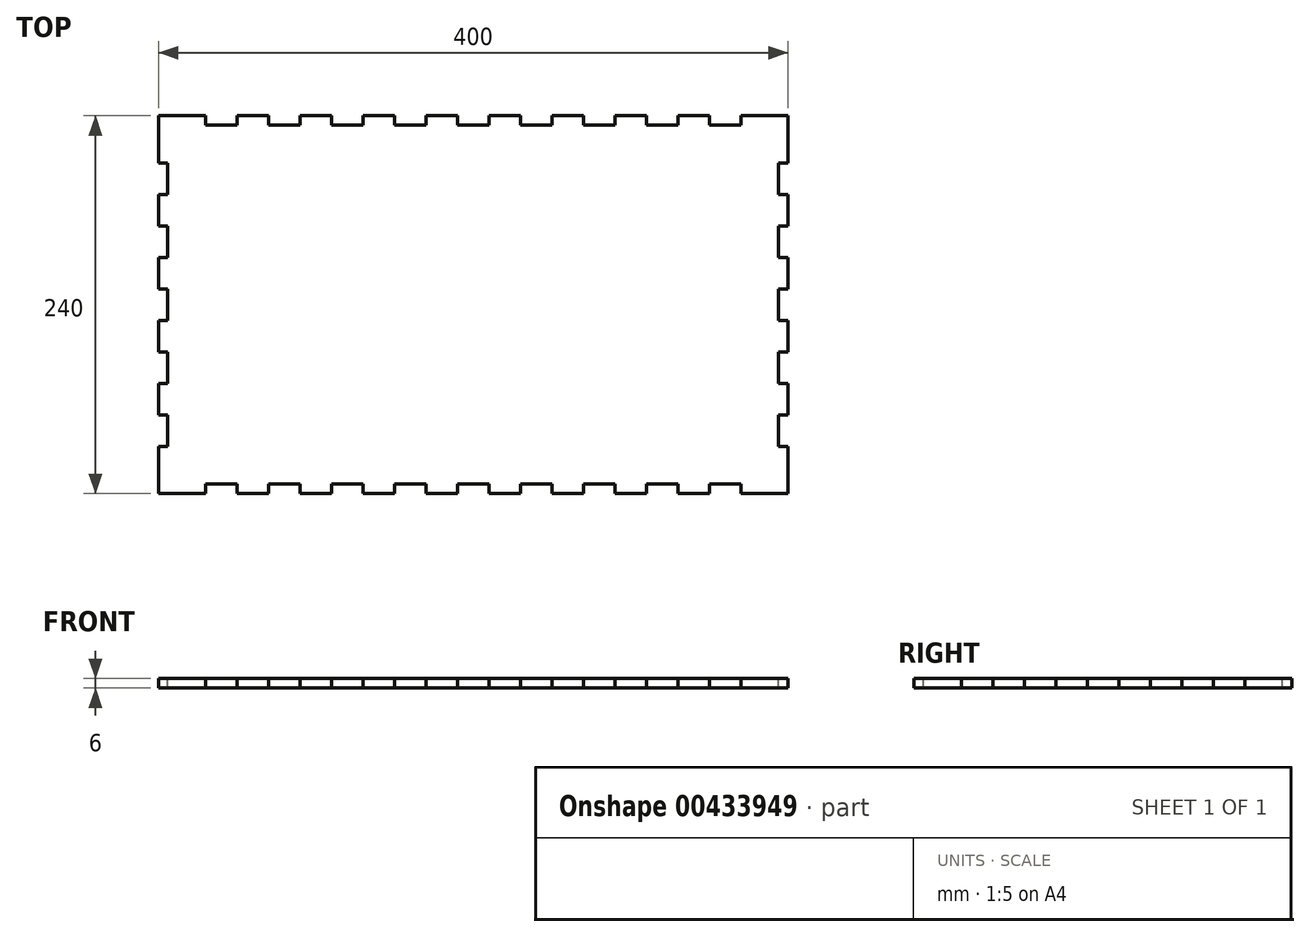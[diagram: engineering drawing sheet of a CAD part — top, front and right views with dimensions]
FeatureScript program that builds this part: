
annotation { "Feature Type Name" : "Feature", "Feature Type Description" : "" }
export const myFeature = defineFeature(function(context is Context, id is Id, definition is map)
    precondition{}
    {
        {
            var Q0;
            Q0=qCreatedBy(makeId("Top.planeOp"),FACE);
            var sketch = newSketch(context, id + "F0", { "sketchPlane" : qUnion([Q0])});
            skLineSegment(sketch, "E0.bottom", {"start": v(200, -120) * mm, "end": v(-200, -120) * mm});
            skLineSegment(sketch, "E0.top", {"start": v(200, 120) * mm, "end": v(-200, 120) * mm});
            skLineSegment(sketch, "E0.left", {"start": v(200, -120) * mm, "end": v(200, 120) * mm});
            skLineSegment(sketch, "E0.right", {"start": v(-200, -120) * mm, "end": v(-200, 120) * mm});
            skPoint(sketch, "E0.middle", {"position": v(0, 0) * mm});
            skSolve(sketch);
        }
        {
            var Q0;
            Q0=makeQuery(id+"F0.imprint","IMPRINT",FACE,{"disambiguationData":[TD([[makeQuery(id+"F0.imprint","IMPRINT",EDGE,{"derivedFrom":sQuery(id+"F0.wireOp",EDGE,"E0.bottom")}),-1.0]])]});
            extrude(context, id + "F1", {"entities" : qUnion([Q0]), "depth" : 6 * mm});
        }
        {
            var Q0;
            Q0=makeQuery(id+"F1.opExtrude","CAP_FACE",FACE,{"disambiguationData":[OSD([sQuery(id+"F0.wireOp",EDGE,"E0.bottom"),sQuery(id+"F0.wireOp",EDGE,"E0.top"),sQuery(id+"F0.wireOp",EDGE,"E0.left"),sQuery(id+"F0.wireOp",EDGE,"E0.right")])],"isStart":false});
            var sketch = newSketch(context, id + "F2", { "sketchPlane" : qUnion([Q0])});
            skLineSegment(sketch, "E1", {"start": v(-200, 90) * mm, "end": v(-194, 90) * mm});
            skLineSegment(sketch, "E2", {"start": v(-194, 90) * mm, "end": v(-194, 70) * mm});
            skLineSegment(sketch, "E3", {"start": v(-194, 70) * mm, "end": v(-200, 70) * mm});
            skLineSegment(sketch, "E4.1.0.0", {"start": v(-200, 50) * mm, "end": v(-194, 50) * mm});
            skLineSegment(sketch, "E4.1.0.1", {"start": v(-194, 50) * mm, "end": v(-194, 30) * mm});
            skLineSegment(sketch, "E4.1.0.2", {"start": v(-194, 30) * mm, "end": v(-200, 30) * mm});
            skLineSegment(sketch, "E4.2.0.0", {"start": v(-200, 10) * mm, "end": v(-194, 10) * mm});
            skLineSegment(sketch, "E4.2.0.1", {"start": v(-194, 10) * mm, "end": v(-194, -10) * mm});
            skLineSegment(sketch, "E4.2.0.2", {"start": v(-194, -10) * mm, "end": v(-200, -10) * mm});
            skLineSegment(sketch, "E4.3.0.0", {"start": v(-200, -30) * mm, "end": v(-194, -30) * mm});
            skLineSegment(sketch, "E4.3.0.1", {"start": v(-194, -30) * mm, "end": v(-194, -50) * mm});
            skLineSegment(sketch, "E4.3.0.2", {"start": v(-194, -50) * mm, "end": v(-200, -50) * mm});
            skLineSegment(sketch, "E4.4.0.0", {"start": v(-200, -70) * mm, "end": v(-194, -70) * mm});
            skLineSegment(sketch, "E4.4.0.1", {"start": v(-194, -70) * mm, "end": v(-194, -90) * mm});
            skLineSegment(sketch, "E4.4.0.2", {"start": v(-194, -90) * mm, "end": v(-200, -90) * mm});
            skLineSegment(sketch, "E4.direction1", {"start": v(-200, 100) * mm, "end": v(-200, 60) * mm, "construction": true});
            skLineSegment(sketch, "E5.MirrorCS", {"start": v(200, 90) * mm, "end": v(194, 90) * mm});
            skLineSegment(sketch, "E6.MirrorCS", {"start": v(194, -90) * mm, "end": v(200, -90) * mm});
            skLineSegment(sketch, "E7.MirrorCS", {"start": v(200, 10) * mm, "end": v(194, 10) * mm});
            skLineSegment(sketch, "E8.MirrorCS", {"start": v(200, -70) * mm, "end": v(194, -70) * mm});
            skLineSegment(sketch, "E9.MirrorCS", {"start": v(194, 30) * mm, "end": v(200, 30) * mm});
            skLineSegment(sketch, "E10.MirrorCS", {"start": v(194, -50) * mm, "end": v(200, -50) * mm});
            skLineSegment(sketch, "E11.MirrorCS", {"start": v(200, 50) * mm, "end": v(194, 50) * mm});
            skLineSegment(sketch, "E12.MirrorCS", {"start": v(194, 70) * mm, "end": v(200, 70) * mm});
            skLineSegment(sketch, "E13.MirrorCS", {"start": v(200, -30) * mm, "end": v(194, -30) * mm});
            skLineSegment(sketch, "E14.MirrorCS", {"start": v(194, -10) * mm, "end": v(200, -10) * mm});
            skLineSegment(sketch, "E15.MirrorCS", {"start": v(194, 90) * mm, "end": v(194, 70) * mm});
            skLineSegment(sketch, "E16.MirrorCS", {"start": v(194, -70) * mm, "end": v(194, -90) * mm});
            skLineSegment(sketch, "E17.MirrorCS", {"start": v(194, 50) * mm, "end": v(194, 30) * mm});
            skLineSegment(sketch, "E18.MirrorCS", {"start": v(194, -30) * mm, "end": v(194, -50) * mm});
            skLineSegment(sketch, "E19.MirrorCS", {"start": v(194, 10) * mm, "end": v(194, -10) * mm});
            skLineSegment(sketch, "E20", {"start": v(-170, 120) * mm, "end": v(-170, 114) * mm});
            skLineSegment(sketch, "E21", {"start": v(-170, 114) * mm, "end": v(-150, 114) * mm});
            skLineSegment(sketch, "E22", {"start": v(-150, 114) * mm, "end": v(-150, 120) * mm});
            skLineSegment(sketch, "E23.1.0.0", {"start": v(-130, 114) * mm, "end": v(-110, 114) * mm});
            skLineSegment(sketch, "E23.1.0.1", {"start": v(-110, 114) * mm, "end": v(-110, 120) * mm});
            skLineSegment(sketch, "E23.1.0.2", {"start": v(-130, 120) * mm, "end": v(-130, 114) * mm});
            skLineSegment(sketch, "E23.2.0.0", {"start": v(-90, 114) * mm, "end": v(-70, 114) * mm});
            skLineSegment(sketch, "E23.2.0.1", {"start": v(-70, 114) * mm, "end": v(-70, 120) * mm});
            skLineSegment(sketch, "E23.2.0.2", {"start": v(-90, 120) * mm, "end": v(-90, 114) * mm});
            skLineSegment(sketch, "E23.3.0.0", {"start": v(-50, 114) * mm, "end": v(-30, 114) * mm});
            skLineSegment(sketch, "E23.3.0.1", {"start": v(-30, 114) * mm, "end": v(-30, 120) * mm});
            skLineSegment(sketch, "E23.3.0.2", {"start": v(-50, 120) * mm, "end": v(-50, 114) * mm});
            skLineSegment(sketch, "E23.4.0.0", {"start": v(-10, 114) * mm, "end": v(10, 114) * mm});
            skLineSegment(sketch, "E23.4.0.1", {"start": v(10, 114) * mm, "end": v(10, 120) * mm});
            skLineSegment(sketch, "E23.4.0.2", {"start": v(-10, 120) * mm, "end": v(-10, 114) * mm});
            skLineSegment(sketch, "E23.5.0.0", {"start": v(30, 114) * mm, "end": v(50, 114) * mm});
            skLineSegment(sketch, "E23.5.0.1", {"start": v(50, 114) * mm, "end": v(50, 120) * mm});
            skLineSegment(sketch, "E23.5.0.2", {"start": v(30, 120) * mm, "end": v(30, 114) * mm});
            skLineSegment(sketch, "E23.6.0.0", {"start": v(70, 114) * mm, "end": v(90, 114) * mm});
            skLineSegment(sketch, "E23.6.0.1", {"start": v(90, 114) * mm, "end": v(90, 120) * mm});
            skLineSegment(sketch, "E23.6.0.2", {"start": v(70, 120) * mm, "end": v(70, 114) * mm});
            skLineSegment(sketch, "E23.7.0.0", {"start": v(110, 114) * mm, "end": v(130, 114) * mm});
            skLineSegment(sketch, "E23.7.0.1", {"start": v(130, 114) * mm, "end": v(130, 120) * mm});
            skLineSegment(sketch, "E23.7.0.2", {"start": v(110, 120) * mm, "end": v(110, 114) * mm});
            skLineSegment(sketch, "E23.8.0.0", {"start": v(150, 114) * mm, "end": v(170, 114) * mm});
            skLineSegment(sketch, "E23.8.0.1", {"start": v(170, 114) * mm, "end": v(170, 120) * mm});
            skLineSegment(sketch, "E23.8.0.2", {"start": v(150, 120) * mm, "end": v(150, 114) * mm});
            skLineSegment(sketch, "E23.direction1", {"start": v(-170, 114) * mm, "end": v(-130, 114) * mm, "construction": true});
            skLineSegment(sketch, "E24.MirrorCS", {"start": v(-130, -120) * mm, "end": v(-130, -114) * mm});
            skLineSegment(sketch, "E25.MirrorCS", {"start": v(-170, -120) * mm, "end": v(-170, -114) * mm});
            skLineSegment(sketch, "E26.MirrorCS", {"start": v(70, -120) * mm, "end": v(70, -114) * mm});
            skLineSegment(sketch, "E27.MirrorCS", {"start": v(-110, -114) * mm, "end": v(-110, -120) * mm});
            skLineSegment(sketch, "E28.MirrorCS", {"start": v(-50, -120) * mm, "end": v(-50, -114) * mm});
            skLineSegment(sketch, "E29.MirrorCS", {"start": v(90, -114) * mm, "end": v(90, -120) * mm});
            skLineSegment(sketch, "E30.MirrorCS", {"start": v(-30, -114) * mm, "end": v(-30, -120) * mm});
            skLineSegment(sketch, "E31.MirrorCS", {"start": v(150, -120) * mm, "end": v(150, -114) * mm});
            skLineSegment(sketch, "E32.MirrorCS", {"start": v(170, -114) * mm, "end": v(170, -120) * mm});
            skLineSegment(sketch, "E33.MirrorCS", {"start": v(-10, -120) * mm, "end": v(-10, -114) * mm});
            skLineSegment(sketch, "E34.MirrorCS", {"start": v(-150, -114) * mm, "end": v(-150, -120) * mm});
            skLineSegment(sketch, "E35.MirrorCS", {"start": v(10, -114) * mm, "end": v(10, -120) * mm});
            skLineSegment(sketch, "E36.MirrorCS", {"start": v(-90, -120) * mm, "end": v(-90, -114) * mm});
            skLineSegment(sketch, "E37.MirrorCS", {"start": v(30, -120) * mm, "end": v(30, -114) * mm});
            skLineSegment(sketch, "E38.MirrorCS", {"start": v(110, -120) * mm, "end": v(110, -114) * mm});
            skLineSegment(sketch, "E39.MirrorCS", {"start": v(50, -114) * mm, "end": v(50, -120) * mm});
            skLineSegment(sketch, "E40.MirrorCS", {"start": v(-70, -114) * mm, "end": v(-70, -120) * mm});
            skLineSegment(sketch, "E41.MirrorCS", {"start": v(130, -114) * mm, "end": v(130, -120) * mm});
            skLineSegment(sketch, "E42.MirrorCS", {"start": v(-170, -114) * mm, "end": v(-150, -114) * mm});
            skLineSegment(sketch, "E43.MirrorCS", {"start": v(-170, -114) * mm, "end": v(-130, -114) * mm, "construction": true});
            skLineSegment(sketch, "E44.MirrorCS", {"start": v(-130, -114) * mm, "end": v(-110, -114) * mm});
            skLineSegment(sketch, "E45.MirrorCS", {"start": v(-50, -114) * mm, "end": v(-30, -114) * mm});
            skLineSegment(sketch, "E46.MirrorCS", {"start": v(-10, -114) * mm, "end": v(10, -114) * mm});
            skLineSegment(sketch, "E47.MirrorCS", {"start": v(110, -114) * mm, "end": v(130, -114) * mm});
            skLineSegment(sketch, "E48.MirrorCS", {"start": v(-90, -114) * mm, "end": v(-70, -114) * mm});
            skLineSegment(sketch, "E49.MirrorCS", {"start": v(150, -114) * mm, "end": v(170, -114) * mm});
            skLineSegment(sketch, "E50.MirrorCS", {"start": v(70, -114) * mm, "end": v(90, -114) * mm});
            skLineSegment(sketch, "E51.MirrorCS", {"start": v(30, -114) * mm, "end": v(50, -114) * mm});
            skSolve(sketch);
        }
        {
            var Q0;
            {var subQ0=sQuery(id+"F2.wireOp",EDGE,"E1");Q0=makeQuery(id+"F2.imprint","IMPRINT",FACE,{"disambiguationData":[TD([[makeQuery(id+"F2.imprint","IMPRINT",EDGE,{"derivedFrom":subQ0}),-1.0]])]});}
            var Q1;
            {var subQ0=sQuery(id+"F2.wireOp",EDGE,"E4.1.0.0");Q1=makeQuery(id+"F2.imprint","IMPRINT",FACE,{"disambiguationData":[TD([[makeQuery(id+"F2.imprint","IMPRINT",EDGE,{"derivedFrom":subQ0}),-1.0]])]});}
            var Q2;
            {var subQ0=sQuery(id+"F2.wireOp",EDGE,"E4.3.0.0");Q2=makeQuery(id+"F2.imprint","IMPRINT",FACE,{"disambiguationData":[TD([[makeQuery(id+"F2.imprint","IMPRINT",EDGE,{"derivedFrom":subQ0}),-1.0]])]});}
            var Q3;
            {var subQ0=sQuery(id+"F2.wireOp",EDGE,"E4.2.0.0");Q3=makeQuery(id+"F2.imprint","IMPRINT",FACE,{"disambiguationData":[TD([[makeQuery(id+"F2.imprint","IMPRINT",EDGE,{"derivedFrom":subQ0}),-1.0]])]});}
            var Q4;
            {var subQ0=sQuery(id+"F2.wireOp",EDGE,"E4.4.0.0");Q4=makeQuery(id+"F2.imprint","IMPRINT",FACE,{"disambiguationData":[TD([[makeQuery(id+"F2.imprint","IMPRINT",EDGE,{"derivedFrom":subQ0}),-1.0]])]});}
            var Q5;
            {var subQ0=sQuery(id+"F2.wireOp",EDGE,"E20");Q5=makeQuery(id+"F2.imprint","IMPRINT",FACE,{"disambiguationData":[TD([[makeQuery(id+"F2.imprint","IMPRINT",EDGE,{"derivedFrom":subQ0}),1.0]])]});}
            var Q6;
            Q6=makeQuery(id+"F2.imprint","IMPRINT",FACE,{"disambiguationData":[TD([[makeQuery(id+"F2.imprint","IMPRINT",EDGE,{"derivedFrom":sQuery(id+"F2.wireOp",EDGE,"E23.1.0.0")}),1.0]])]});
            var Q7;
            Q7=makeQuery(id+"F2.imprint","IMPRINT",FACE,{"disambiguationData":[TD([[makeQuery(id+"F2.imprint","IMPRINT",EDGE,{"derivedFrom":sQuery(id+"F2.wireOp",EDGE,"E23.2.0.0")}),1.0]])]});
            var Q8;
            Q8=makeQuery(id+"F2.imprint","IMPRINT",FACE,{"disambiguationData":[TD([[makeQuery(id+"F2.imprint","IMPRINT",EDGE,{"derivedFrom":sQuery(id+"F2.wireOp",EDGE,"E23.3.0.0")}),1.0]])]});
            var Q9;
            Q9=makeQuery(id+"F2.imprint","IMPRINT",FACE,{"disambiguationData":[TD([[makeQuery(id+"F2.imprint","IMPRINT",EDGE,{"derivedFrom":sQuery(id+"F2.wireOp",EDGE,"E23.4.0.0")}),1.0]])]});
            var Q10;
            Q10=makeQuery(id+"F2.imprint","IMPRINT",FACE,{"disambiguationData":[TD([[makeQuery(id+"F2.imprint","IMPRINT",EDGE,{"derivedFrom":sQuery(id+"F2.wireOp",EDGE,"E23.5.0.0")}),1.0]])]});
            var Q11;
            Q11=makeQuery(id+"F2.imprint","IMPRINT",FACE,{"disambiguationData":[TD([[makeQuery(id+"F2.imprint","IMPRINT",EDGE,{"derivedFrom":sQuery(id+"F2.wireOp",EDGE,"E23.6.0.0")}),1.0]])]});
            var Q12;
            Q12=makeQuery(id+"F2.imprint","IMPRINT",FACE,{"disambiguationData":[TD([[makeQuery(id+"F2.imprint","IMPRINT",EDGE,{"derivedFrom":sQuery(id+"F2.wireOp",EDGE,"E23.7.0.0")}),1.0]])]});
            var Q13;
            Q13=makeQuery(id+"F2.imprint","IMPRINT",FACE,{"disambiguationData":[TD([[makeQuery(id+"F2.imprint","IMPRINT",EDGE,{"derivedFrom":sQuery(id+"F2.wireOp",EDGE,"E23.8.0.0")}),1.0]])]});
            var Q14;
            {var subQ0=sQuery(id+"F2.wireOp",EDGE,"E5.MirrorCS");Q14=makeQuery(id+"F2.imprint","IMPRINT",FACE,{"disambiguationData":[TD([[makeQuery(id+"F2.imprint","IMPRINT",EDGE,{"derivedFrom":subQ0}),1.0]])]});}
            var Q15;
            {var subQ0=sQuery(id+"F2.wireOp",EDGE,"E9.MirrorCS");Q15=makeQuery(id+"F2.imprint","IMPRINT",FACE,{"disambiguationData":[TD([[makeQuery(id+"F2.imprint","IMPRINT",EDGE,{"derivedFrom":subQ0}),1.0]])]});}
            var Q16;
            {var subQ0=sQuery(id+"F2.wireOp",EDGE,"E7.MirrorCS");Q16=makeQuery(id+"F2.imprint","IMPRINT",FACE,{"disambiguationData":[TD([[makeQuery(id+"F2.imprint","IMPRINT",EDGE,{"derivedFrom":subQ0}),1.0]])]});}
            var Q17;
            {var subQ0=sQuery(id+"F2.wireOp",EDGE,"E10.MirrorCS");Q17=makeQuery(id+"F2.imprint","IMPRINT",FACE,{"disambiguationData":[TD([[makeQuery(id+"F2.imprint","IMPRINT",EDGE,{"derivedFrom":subQ0}),1.0]])]});}
            var Q18;
            {var subQ0=sQuery(id+"F2.wireOp",EDGE,"E6.MirrorCS");Q18=makeQuery(id+"F2.imprint","IMPRINT",FACE,{"disambiguationData":[TD([[makeQuery(id+"F2.imprint","IMPRINT",EDGE,{"derivedFrom":subQ0}),1.0]])]});}
            var Q19;
            {var subQ0=sQuery(id+"F2.wireOp",EDGE,"E25.MirrorCS");Q19=makeQuery(id+"F2.imprint","IMPRINT",FACE,{"disambiguationData":[TD([[makeQuery(id+"F2.imprint","IMPRINT",EDGE,{"derivedFrom":subQ0}),-1.0]])]});}
            var Q20;
            {var subQ0=sQuery(id+"F2.wireOp",EDGE,"E24.MirrorCS");Q20=makeQuery(id+"F2.imprint","IMPRINT",FACE,{"disambiguationData":[TD([[makeQuery(id+"F2.imprint","IMPRINT",EDGE,{"derivedFrom":subQ0}),-1.0]])]});}
            var Q21;
            {var subQ0=sQuery(id+"F2.wireOp",EDGE,"E36.MirrorCS");Q21=makeQuery(id+"F2.imprint","IMPRINT",FACE,{"disambiguationData":[TD([[makeQuery(id+"F2.imprint","IMPRINT",EDGE,{"derivedFrom":subQ0}),-1.0]])]});}
            var Q22;
            {var subQ0=sQuery(id+"F2.wireOp",EDGE,"E28.MirrorCS");Q22=makeQuery(id+"F2.imprint","IMPRINT",FACE,{"disambiguationData":[TD([[makeQuery(id+"F2.imprint","IMPRINT",EDGE,{"derivedFrom":subQ0}),-1.0]])]});}
            var Q23;
            {var subQ0=sQuery(id+"F2.wireOp",EDGE,"E33.MirrorCS");Q23=makeQuery(id+"F2.imprint","IMPRINT",FACE,{"disambiguationData":[TD([[makeQuery(id+"F2.imprint","IMPRINT",EDGE,{"derivedFrom":subQ0}),-1.0]])]});}
            var Q24;
            {var subQ0=sQuery(id+"F2.wireOp",EDGE,"E37.MirrorCS");Q24=makeQuery(id+"F2.imprint","IMPRINT",FACE,{"disambiguationData":[TD([[makeQuery(id+"F2.imprint","IMPRINT",EDGE,{"derivedFrom":subQ0}),-1.0]])]});}
            var Q25;
            {var subQ0=sQuery(id+"F2.wireOp",EDGE,"E26.MirrorCS");Q25=makeQuery(id+"F2.imprint","IMPRINT",FACE,{"disambiguationData":[TD([[makeQuery(id+"F2.imprint","IMPRINT",EDGE,{"derivedFrom":subQ0}),-1.0]])]});}
            var Q26;
            {var subQ0=sQuery(id+"F2.wireOp",EDGE,"E38.MirrorCS");Q26=makeQuery(id+"F2.imprint","IMPRINT",FACE,{"disambiguationData":[TD([[makeQuery(id+"F2.imprint","IMPRINT",EDGE,{"derivedFrom":subQ0}),-1.0]])]});}
            var Q27;
            {var subQ0=sQuery(id+"F2.wireOp",EDGE,"E31.MirrorCS");Q27=makeQuery(id+"F2.imprint","IMPRINT",FACE,{"disambiguationData":[TD([[makeQuery(id+"F2.imprint","IMPRINT",EDGE,{"derivedFrom":subQ0}),-1.0]])]});}
            extrude(context, id + "F3", {"entities" : qUnion([Q0, Q1, Q2, Q3, Q4, Q5, Q6, Q7, Q8, Q9, Q10, Q11, Q12, Q13, Q14, Q15, Q16, Q17, Q18, Q19, Q20, Q21, Q22, Q23, Q24, Q25, Q26, Q27]), "operationType" : NewBodyOperationType.REMOVE, "oppositeDirection" : true, "depth" : 25 * mm});
        }
    });
